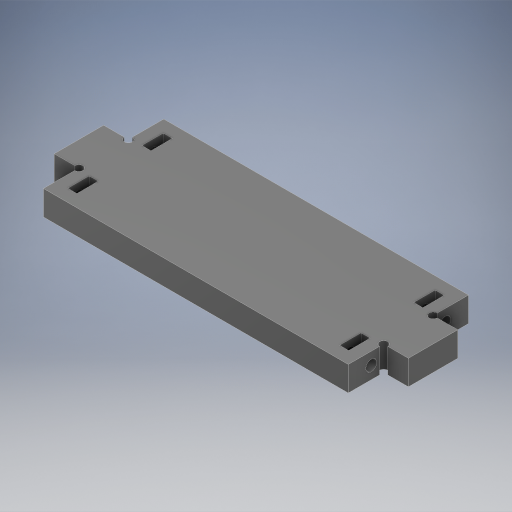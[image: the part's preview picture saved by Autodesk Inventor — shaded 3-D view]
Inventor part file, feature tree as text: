
AUTODESK INVENTOR PART (.ipt)
format: ipt  version: 2024 (Build 280153000, 153)  size: 359,936 bytes
history: native  units: in
note: dims shown in document units (in); Inventor stores cm internally (conversion verified against a paired STEP export)
features: projected_geometry x6, extrude x5, sketch x5, other x4
ambient origin geometry x4: Origin, X Axis, Y Axis, Z Axis
bodies: Body1 (feature_tree)
feature tree (20):
  other  "솔리드1"
  extrude  "돌출1"  Depth=2.9134in
  extrude  "돌출2"  Depth=1.1496in
  extrude  "돌출3"  Depth=0.2362in
  extrude  "돌출4"  Depth=0.4724in
  extrude  "돌출5"  Depth=0.2362in
  other  "우측면도"
  other  "평면도"
  other  "정면도"
  sketch  "스케치1"
  sketch  "스케치2"
  projected_geometry  "투영된 루프1"
  projected_geometry  "투영된 루프2"
  sketch  "스케치3"
  projected_geometry  "투영된 루프3"
  projected_geometry  "투영된 루프4"
  sketch  "스케치4"
  projected_geometry  "투영된 루프5"
  sketch  "스케치5"
  projected_geometry  "투영된 루프6"
